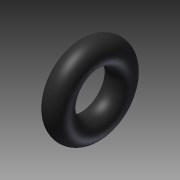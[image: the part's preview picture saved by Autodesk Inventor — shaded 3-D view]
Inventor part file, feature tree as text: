
AUTODESK INVENTOR PART (.ipt)
format: ipt  version: 2012 SP1 (Build 160190100, 190)  size: 175,104 bytes
history: native  units: in
note: dims shown in document units (in); Inventor stores cm internally (conversion verified against a paired STEP export)
features: sketch x2, sweep x1
ambient origin geometry x8: Origin, YZ Plane, XZ Plane, XY Plane, X Axis, Y Axis, Z Axis, Center Point
bodies: Solid1 (feature_tree)
feature tree (3):
  sweep  "Sweep1"
  sketch  "Sketch1"  dims[d0=0.07in d1=0.114in]
  sketch  "Sketch2"  dims[d3=0.0in]
